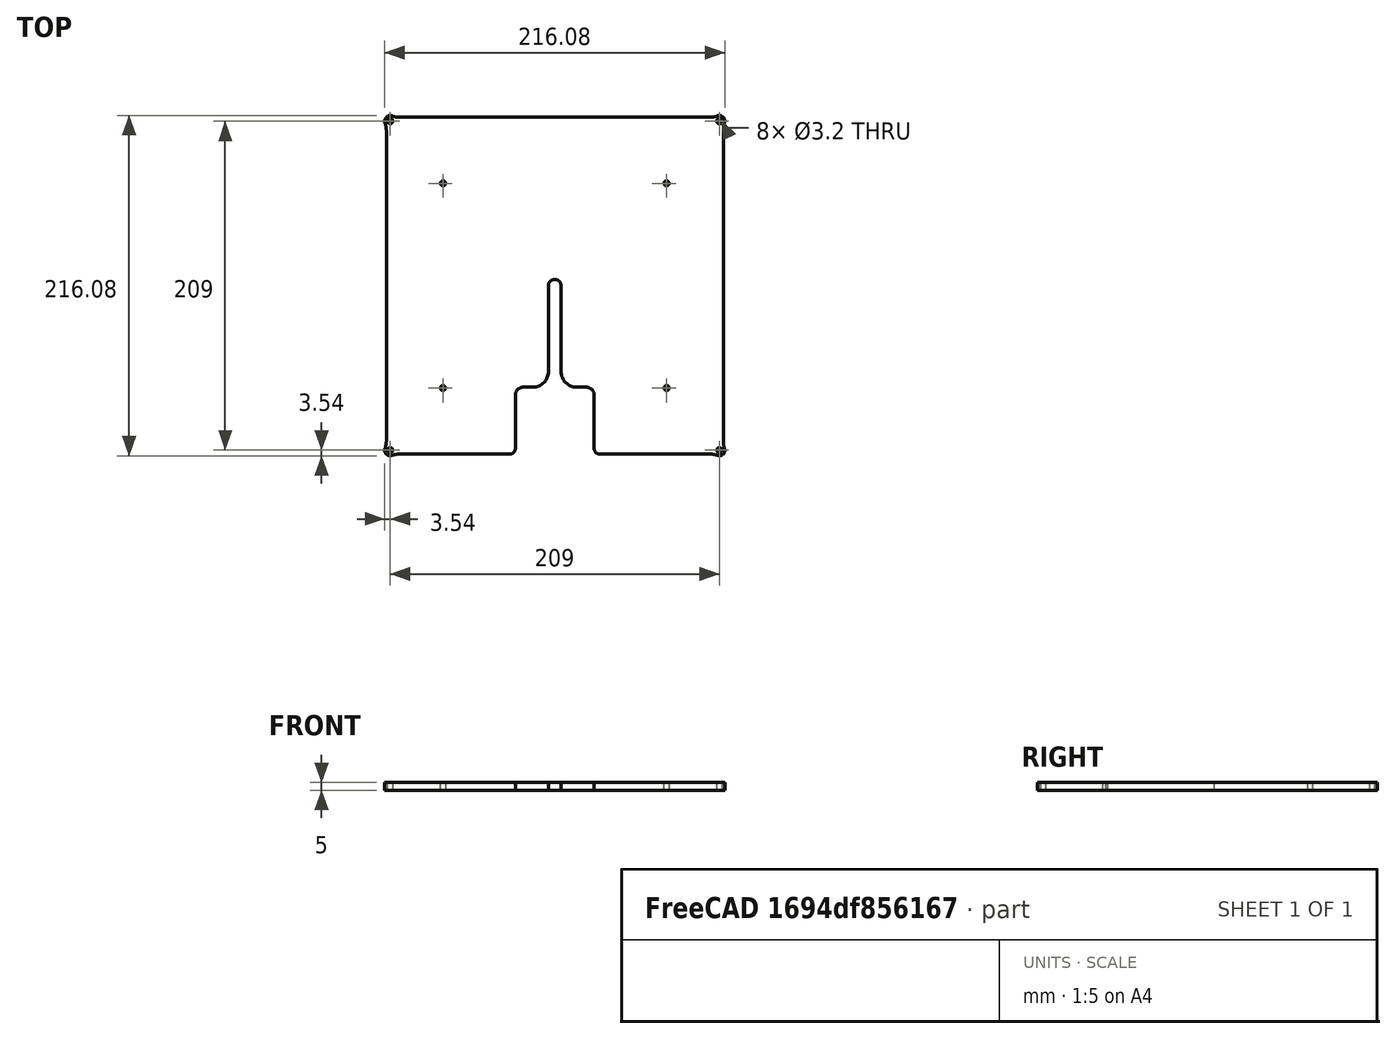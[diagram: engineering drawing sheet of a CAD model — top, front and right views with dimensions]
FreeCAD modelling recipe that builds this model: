
FCSTD DOCUMENT  (FreeCAD 0.17R13541 (Git))
Label: xx_1044_build-surface-base
License: All rights reserved
LicenseURL: http://en.wikipedia.org/wiki/All_rights_reserved
objects: Sketcher::SketchObject×1, PartDesign::Pad×1, PartDesign::Body×1
note: 4 computed .brp shape members not serialized (recipe doc carries the construction recipe); baked Part::Feature solids carry a one-line shape summary decoded from their .brp

FEATURE [Sketcher::SketchObject] Sketch038
  MapMode = 5
  Support = -> [XY_Plane]
  sketch-geometry (38):
    g0: Circle CenterX=104.5 CenterY=-104.5 CenterZ=0 NormalX=0 NormalY=0 NormalZ=-1 AngleXU=0 Radius=1.6
    g1: ArcOfCircle CenterX=0 CenterY=0 CenterZ=0 NormalX=0 NormalY=0 NormalZ=1 AngleXU=0 Radius=4 StartAngle=0 EndAngle=3.14159
    g2: ArcOfCircle CenterX=-98.923 CenterY=-119 CenterZ=0 NormalX=0 NormalY=0 NormalZ=1 AngleXU=0 Radius=12 StartAngle=1.5708 EndAngle=1.93797
    g3: LineSegment StartX=107 StartY=-98.923 StartZ=0 EndX=107 EndY=98.923 EndZ=0
    g4: Circle CenterX=104.5 CenterY=104.5 CenterZ=0 NormalX=0 NormalY=0 NormalZ=-1 AngleXU=0 Radius=1.6
    g5: ArcOfCircle CenterX=98.923 CenterY=119 CenterZ=0 NormalX=0 NormalY=0 NormalZ=1 AngleXU=0 Radius=12 StartAngle=4.71239 EndAngle=5.07957
    g6: ArcOfCircle CenterX=-104.5 CenterY=-104.5 CenterZ=0 NormalX=0 NormalY=0 NormalZ=1 AngleXU=0 Radius=3.53553 StartAngle=2.77441 EndAngle=5.07957
    g7: ArcOfCircle CenterX=119 CenterY=-98.923 CenterZ=0 NormalX=0 NormalY=0 NormalZ=1 AngleXU=0 Radius=12 StartAngle=3.14159 EndAngle=3.50877
    g8: ArcOfCircle CenterX=119 CenterY=98.923 CenterZ=0 NormalX=0 NormalY=0 NormalZ=1 AngleXU=0 Radius=12 StartAngle=2.77441 EndAngle=3.14159
    g9: ArcOfCircle CenterX=104.5 CenterY=-104.5 CenterZ=0 NormalX=0 NormalY=0 NormalZ=1 AngleXU=0 Radius=3.53553 StartAngle=4.34521 EndAngle=6.65036
    g10: LineSegment StartX=-98.923 StartY=-107 StartZ=0 EndX=-28.54 EndY=-107 EndZ=0
    g11: Circle CenterX=-104.5 CenterY=-104.5 CenterZ=0 NormalX=0 NormalY=0 NormalZ=-1 AngleXU=0 Radius=1.6
    g12: LineSegment StartX=98.923 StartY=107 StartZ=0 EndX=-98.923 EndY=107 EndZ=0
    g13: LineSegment StartX=-4 StartY=0 StartZ=0 EndX=-4 EndY=-54.5 EndZ=0
    g14: Circle CenterX=71 CenterY=-65 CenterZ=0 NormalX=0 NormalY=0 NormalZ=-1 AngleXU=0 Radius=1.6
    g15: ArcOfCircle CenterX=-104.5 CenterY=104.5 CenterZ=0 NormalX=0 NormalY=0 NormalZ=1 AngleXU=0 Radius=3.53553 StartAngle=1.20362 EndAngle=3.50877
    g16: LineSegment StartX=-107 StartY=98.923 StartZ=0 EndX=-107 EndY=-98.923 EndZ=0
    g17: ArcOfCircle CenterX=-98.923 CenterY=119 CenterZ=0 NormalX=0 NormalY=0 NormalZ=1 AngleXU=0 Radius=12 StartAngle=4.34521 EndAngle=4.71239
    g18: LineSegment StartX=28.54 StartY=-107 StartZ=0 EndX=98.923 EndY=-107 EndZ=0
    g19: Circle CenterX=71 CenterY=65 CenterZ=0 NormalX=0 NormalY=0 NormalZ=-1 AngleXU=0 Radius=1.6
    g20: ArcOfCircle CenterX=98.923 CenterY=-119 CenterZ=0 NormalX=0 NormalY=0 NormalZ=1 AngleXU=0 Radius=12 StartAngle=1.20362 EndAngle=1.5708
    g21: ArcOfCircle CenterX=-14 CenterY=-54.5 CenterZ=0 NormalX=0 NormalY=0 NormalZ=1 AngleXU=0 Radius=10 StartAngle=4.71239 EndAngle=6.28319
    g22: LineSegment StartX=20 StartY=-64.5 StartZ=0 EndX=14 EndY=-64.5 EndZ=0
    g23: ArcOfCircle CenterX=-28.54 CenterY=-103.46 CenterZ=0 NormalX=0 NormalY=0 NormalZ=1 AngleXU=0 Radius=3.54 StartAngle=4.71239 EndAngle=6.28319
    g24: LineSegment StartX=-25 StartY=-69.5 StartZ=0 EndX=-25 EndY=-103.46 EndZ=0
    g25: Circle CenterX=-104.5 CenterY=104.5 CenterZ=0 NormalX=0 NormalY=0 NormalZ=-1 AngleXU=0 Radius=1.6
    g26: ArcOfCircle CenterX=14 CenterY=-54.5 CenterZ=0 NormalX=0 NormalY=0 NormalZ=1 AngleXU=0 Radius=10 StartAngle=3.14159 EndAngle=4.71239
    g27: LineSegment StartX=4 StartY=-54.5 StartZ=0 EndX=4 EndY=0 EndZ=0
    g28: ArcOfCircle CenterX=104.5 CenterY=104.5 CenterZ=0 NormalX=0 NormalY=0 NormalZ=1 AngleXU=0 Radius=3.53553 StartAngle=5.91601 EndAngle=8.22116
    g29: ArcOfCircle CenterX=28.54 CenterY=-103.46 CenterZ=0 NormalX=0 NormalY=0 NormalZ=1 AngleXU=0 Radius=3.54 StartAngle=3.14159 EndAngle=4.71239
    g30: ArcOfCircle CenterX=-119 CenterY=-98.923 CenterZ=0 NormalX=0 NormalY=0 NormalZ=1 AngleXU=0 Radius=12 StartAngle=5.91601 EndAngle=6.28319
    g31: LineSegment StartX=-14 StartY=-64.5 StartZ=0 EndX=-20 EndY=-64.5 EndZ=0
    g32: ArcOfCircle CenterX=-119 CenterY=98.923 CenterZ=0 NormalX=0 NormalY=0 NormalZ=1 AngleXU=0 Radius=12 StartAngle=0 EndAngle=0.367178
    g33: ArcOfCircle CenterX=-20 CenterY=-69.5 CenterZ=0 NormalX=0 NormalY=0 NormalZ=1 AngleXU=0 Radius=5 StartAngle=1.5708 EndAngle=3.14159
    g34: Circle CenterX=-71 CenterY=-65 CenterZ=0 NormalX=0 NormalY=0 NormalZ=-1 AngleXU=0 Radius=1.6
    g35: LineSegment StartX=25 StartY=-103.46 StartZ=0 EndX=25 EndY=-69.5 EndZ=0
    g36: Circle CenterX=-71 CenterY=65 CenterZ=0 NormalX=0 NormalY=0 NormalZ=-1 AngleXU=0 Radius=1.6
    g37: ArcOfCircle CenterX=20 CenterY=-69.5 CenterZ=0 NormalX=0 NormalY=0 NormalZ=1 AngleXU=0 Radius=5 StartAngle=0 EndAngle=1.5708
  constraints (30):
    c: Coincident(g30,g6)
    c: Coincident(g32,g15)
    c: Coincident(g30,g16)
    c: Coincident(g16,g32)
    c: Coincident(g2,g6)
    c: Coincident(g17,g15)
    c: Coincident(g10,g2)
    c: Coincident(g17,g12)
    c: Coincident(g23,g10)
    c: Coincident(g23,g24)
    c: Coincident(g24,g33)
    c: Coincident(g31,g33)
    c: Coincident(g21,g31)
    c: Coincident(g21,g13)
    c: Coincident(g1,g13)
    c: Coincident(g26,g27)
    c: Coincident(g27,g1)
    c: Coincident(g26,g22)
    c: Coincident(g37,g22)
    c: Coincident(g35,g29)
    c: Coincident(g37,g35)
    c: Coincident(g18,g29)
    c: Coincident(g20,g18)
    c: Coincident(g12,g5)
    c: Coincident(g9,g20)
    c: Coincident(g5,g28)
    c: Coincident(g7,g3)
    c: Coincident(g8,g3)
    c: Coincident(g7,g9)
    c: Coincident(g8,g28)
FEATURE [PartDesign::Pad] Pad
  Length = 5
  Length2 = 100
  Profile = -> Sketch038
  Type = 0
FEATURE [PartDesign::Body] Body
  Group = -> [Sketch038,Pad]
  Origin = -> Origin
  Tip = -> Pad
